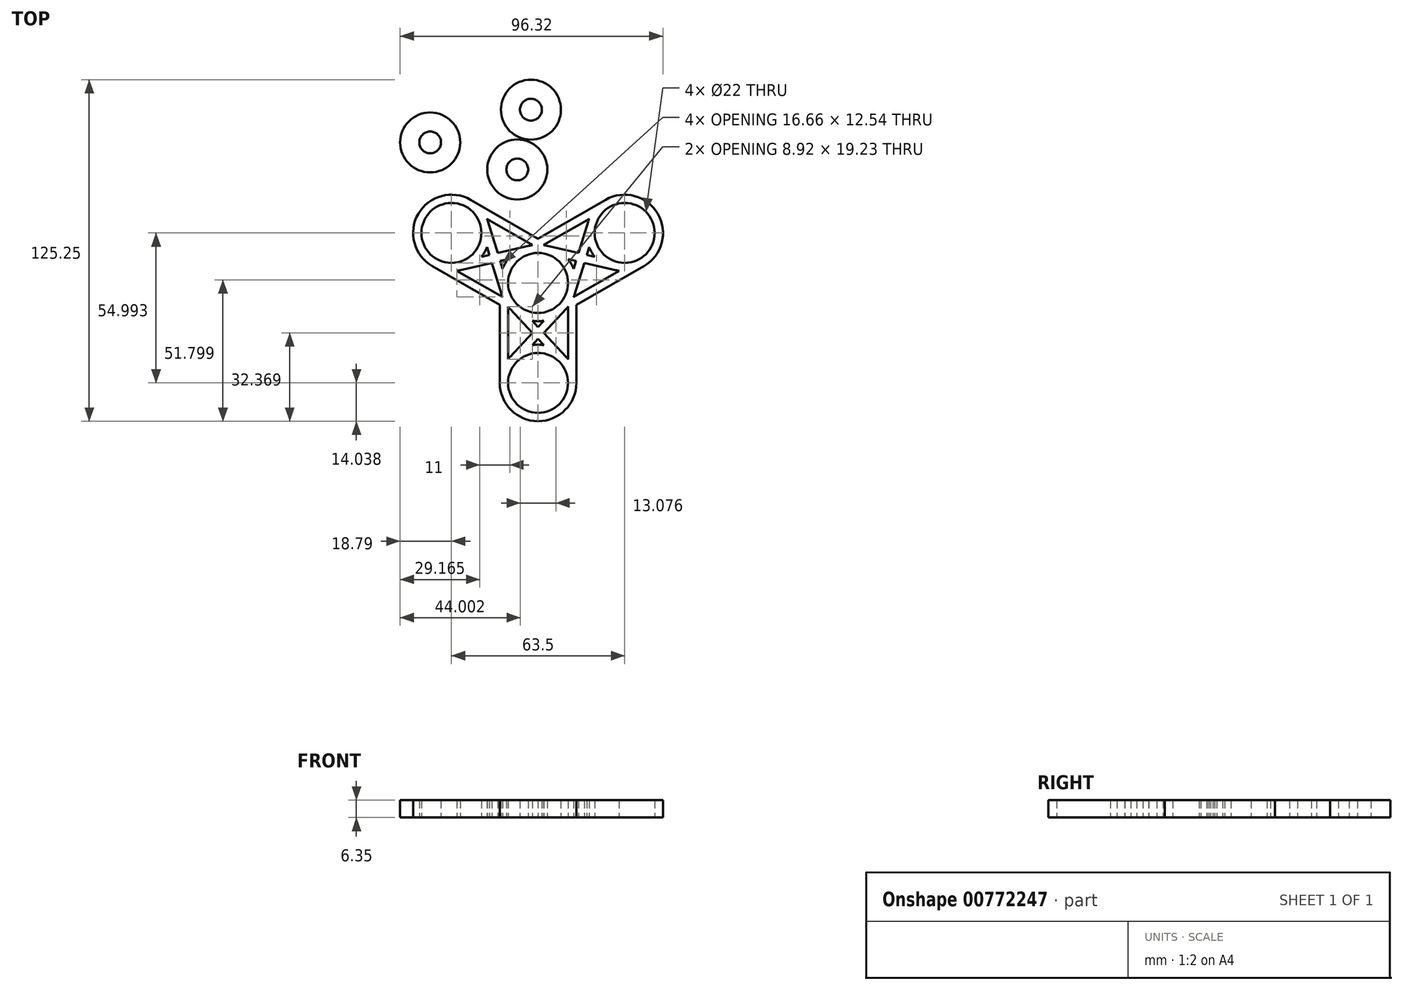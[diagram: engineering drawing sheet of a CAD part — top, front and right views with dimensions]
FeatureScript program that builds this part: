
annotation { "Feature Type Name" : "Feature", "Feature Type Description" : "" }
export const myFeature = defineFeature(function(context is Context, id is Id, definition is map)
    precondition{}
    {
        {
            var Q0;
            Q0=qCreatedBy(makeId("Top.planeOp"),FACE);
            var sketch = newSketch(context, id + "F0", { "sketchPlane" : qUnion([Q0])});
            skCircle(sketch, "E0", {"center": v(0, 0) * mm, "radius": 11 * mm});
            skCircle(sketch, "E1", {"center": v(0, 0) * mm, "radius": 4 * mm});
            skArc(sketch, "E2", {"start": v(-13.42, -4.09) * mm, "mid": v(-13.25, -4.63) * mm, "end": v(-13.05, -5.17) * mm});
            skCircle(sketch, "E3", {"center": v(31.75, 18.33) * mm, "radius": 11 * mm});
            skCircle(sketch, "E4", {"center": v(31.75, 18.33) * mm, "radius": 4 * mm});
            skArc(sketch, "E5", {"start": v(18.69, 13.2) * mm, "mid": v(19.6, 11.31) * mm, "end": v(20.77, 9.59) * mm});
            skCircle(sketch, "E6", {"center": v(-31.75, 18.33) * mm, "radius": 11 * mm});
            skCircle(sketch, "E7", {"center": v(-31.75, 18.33) * mm, "radius": 4 * mm});
            skArc(sketch, "E8", {"start": v(-18.33, 22.42) * mm, "mid": v(-18.5, 22.96) * mm, "end": v(-18.7, 23.5) * mm});
            skCircle(sketch, "E9", {"center": v(0, -36.66) * mm, "radius": 11 * mm});
            skCircle(sketch, "E10", {"center": v(0, -36.66) * mm, "radius": 4 * mm});
            skArc(sketch, "E11", {"start": v(-10.25, -27.08) * mm, "mid": v(-10.64, -27.5) * mm, "end": v(-11, -27.95) * mm});
            skLineSegment(sketch, "E12", {"start": v(-31.75, 18.33) * mm, "end": v(31.75, 18.33) * mm, "construction": true});
            skLineSegment(sketch, "E13", {"start": v(31.75, 18.33) * mm, "end": v(0, -36.66) * mm, "construction": true});
            skLineSegment(sketch, "E14", {"start": v(-31.75, 18.33) * mm, "end": v(0, -36.66) * mm, "construction": true});
            skLineSegment(sketch, "E15", {"start": v(0, 16.2) * mm, "end": v(24.73, 30.48) * mm});
            skLineSegment(sketch, "E16", {"start": v(-14.03, -8.1) * mm, "end": v(-14.03, -36.66) * mm});
            skLineSegment(sketch, "E17", {"start": v(11, -27.95) * mm, "end": v(11, -8.71) * mm});
            skLineSegment(sketch, "E18", {"start": v(14.03, -8.1) * mm, "end": v(38.77, 6.18) * mm});
            skLineSegment(sketch, "E19", {"start": v(-18.7, 23.5) * mm, "end": v(-2.05, 13.88) * mm});
            skLineSegment(sketch, "E20", {"start": v(14.03, -36.66) * mm, "end": v(14.03, -8.1) * mm});
            skLineSegment(sketch, "E21", {"start": v(-18.33, 22.42) * mm, "end": v(-14.84, 10.96) * mm});
            skLineSegment(sketch, "E22", {"start": v(-28.58, 4.66) * mm, "end": v(-16.91, 7.37) * mm});
            skLineSegment(sketch, "E23.trimOffspring", {"start": v(-13.95, 8.05) * mm, "end": v(-10.98, 8.75) * mm});
            skLineSegment(sketch, "E24.trimOffspring", {"start": v(-16.91, 7.37) * mm, "end": v(-13.42, -4.09) * mm});
            skLineSegment(sketch, "E25.trimOffspring", {"start": v(-13.95, 8.05) * mm, "end": v(-13.06, 5.13) * mm});
            skArc(sketch, "E26.trimOffspring", {"start": v(-20.77, 9.59) * mm, "mid": v(-19.6, 11.31) * mm, "end": v(-18.69, 13.2) * mm});
            skLineSegment(sketch, "E27.trimOffspring", {"start": v(-18.69, 13.2) * mm, "end": v(-17.8, 10.28) * mm});
            skArc(sketch, "E28.trimOffspring", {"start": v(-10.98, 8.75) * mm, "mid": v(-12.15, 7.02) * mm, "end": v(-13.06, 5.13) * mm});
            skArc(sketch, "E29.trimOffspring", {"start": v(-29.7, 4.45) * mm, "mid": v(-29.14, 4.54) * mm, "end": v(-28.58, 4.66) * mm});
            skLineSegment(sketch, "E30.trimOffspring", {"start": v(0, 16.2) * mm, "end": v(-24.73, 30.48) * mm});
            skArc(sketch, "E31.trimOffspring", {"start": v(-2.05, 13.88) * mm, "mid": v(-2.61, 13.79) * mm, "end": v(-3.17, 13.67) * mm});
            skLineSegment(sketch, "E32.trimOffspring", {"start": v(2.05, 13.88) * mm, "end": v(18.7, 23.5) * mm});
            skArc(sketch, "E33.trimOffspring", {"start": v(-11, -8.71) * mm, "mid": v(-10.64, -9.16) * mm, "end": v(-10.25, -9.58) * mm});
            skLineSegment(sketch, "E34.trimOffspring", {"start": v(-13.05, -5.17) * mm, "end": v(-29.7, 4.45) * mm});
            skLineSegment(sketch, "E35.trimOffspring", {"start": v(-11, -8.71) * mm, "end": v(-11, -27.95) * mm});
            skLineSegment(sketch, "E36.trimOffspring", {"start": v(-14.03, -8.1) * mm, "end": v(-38.77, 6.18) * mm});
            skLineSegment(sketch, "E37.trimOffspring", {"start": v(13.05, -5.17) * mm, "end": v(29.7, 4.45) * mm});
            skArc(sketch, "E38.trimOffspring", {"start": v(13.05, -5.17) * mm, "mid": v(13.25, -4.63) * mm, "end": v(13.42, -4.09) * mm});
            skLineSegment(sketch, "E39", {"start": v(13.06, 5.13) * mm, "end": v(13.95, 8.05) * mm});
            skLineSegment(sketch, "E40", {"start": v(3.17, 13.67) * mm, "end": v(14.84, 10.96) * mm});
            skLineSegment(sketch, "E41", {"start": v(10.98, 8.75) * mm, "end": v(13.95, 8.05) * mm});
            skLineSegment(sketch, "E42", {"start": v(10.25, -27.08) * mm, "end": v(2.08, -18.33) * mm});
            skLineSegment(sketch, "E43", {"start": v(-10.25, -27.08) * mm, "end": v(-2.08, -18.33) * mm});
            skLineSegment(sketch, "E44.trimOffspring", {"start": v(-20.77, 9.59) * mm, "end": v(-17.8, 10.28) * mm});
            skLineSegment(sketch, "E45.trimOffspring", {"start": v(-14.84, 10.96) * mm, "end": v(-3.17, 13.67) * mm});
            skArc(sketch, "E46.trimOffspring", {"start": v(-24.73, 30.48) * mm, "mid": v(-43.9, 25.35) * mm, "end": v(-38.77, 6.18) * mm});
            skLineSegment(sketch, "E47.trimOffspring", {"start": v(17.8, 10.28) * mm, "end": v(20.77, 9.59) * mm});
            skLineSegment(sketch, "E48.trimOffspring", {"start": v(16.91, 7.37) * mm, "end": v(28.58, 4.66) * mm});
            skLineSegment(sketch, "E49.trimOffspring", {"start": v(14.84, 10.96) * mm, "end": v(18.33, 22.42) * mm});
            skArc(sketch, "E50.trimOffspring", {"start": v(3.17, 13.67) * mm, "mid": v(2.61, 13.79) * mm, "end": v(2.05, 13.88) * mm});
            skArc(sketch, "E51.trimOffspring", {"start": v(13.06, 5.13) * mm, "mid": v(12.15, 7.02) * mm, "end": v(10.98, 8.75) * mm});
            skLineSegment(sketch, "E52.trimOffspring", {"start": v(16.91, 7.37) * mm, "end": v(13.42, -4.09) * mm});
            skLineSegment(sketch, "E53.trimOffspring", {"start": v(18.69, 13.2) * mm, "end": v(17.8, 10.28) * mm});
            skArc(sketch, "E54.trimOffspring", {"start": v(28.58, 4.66) * mm, "mid": v(29.14, 4.54) * mm, "end": v(29.7, 4.45) * mm});
            skArc(sketch, "E55.trimOffspring", {"start": v(38.77, 6.18) * mm, "mid": v(43.9, 25.35) * mm, "end": v(24.73, 30.48) * mm});
            skArc(sketch, "E56.trimOffspring", {"start": v(18.7, 23.5) * mm, "mid": v(18.5, 22.96) * mm, "end": v(18.33, 22.42) * mm});
            skArc(sketch, "E57.trimOffspring", {"start": v(-2.09, -13.88) * mm, "mid": v(0, -14.03) * mm, "end": v(2.09, -13.88) * mm});
            skArc(sketch, "E58.trimOffspring", {"start": v(10.25, -9.58) * mm, "mid": v(10.64, -9.16) * mm, "end": v(11, -8.71) * mm});
            skLineSegment(sketch, "E59.trimOffspring", {"start": v(0, -16.1) * mm, "end": v(2.09, -13.88) * mm});
            skLineSegment(sketch, "E60.trimOffspring", {"start": v(0, -16.1) * mm, "end": v(-2.09, -13.88) * mm});
            skLineSegment(sketch, "E61.trimOffspring", {"start": v(2.08, -18.33) * mm, "end": v(10.25, -9.58) * mm});
            skLineSegment(sketch, "E62.trimOffspring", {"start": v(-2.08, -18.33) * mm, "end": v(-10.25, -9.58) * mm});
            skLineSegment(sketch, "E63.trimOffspring", {"start": v(-2.09, -22.78) * mm, "end": v(0, -20.55) * mm});
            skLineSegment(sketch, "E64.trimOffspring", {"start": v(2.09, -22.78) * mm, "end": v(0, -20.55) * mm});
            skArc(sketch, "E65.trimOffspring", {"start": v(2.09, -22.78) * mm, "mid": v(0, -22.63) * mm, "end": v(-2.09, -22.78) * mm});
            skArc(sketch, "E66.trimOffspring", {"start": v(11, -27.95) * mm, "mid": v(10.64, -27.5) * mm, "end": v(10.25, -27.08) * mm});
            skArc(sketch, "E67.trimOffspring", {"start": v(-14.03, -36.66) * mm, "mid": v(0, -50.7) * mm, "end": v(14.03, -36.66) * mm});
            skLineSegment(sketch, "E68", {"start": v(31.75, 18.33) * mm, "end": v(0, 0) * mm, "construction": true});
            skLineSegment(sketch, "E69", {"start": v(-31.75, 18.33) * mm, "end": v(0, 0) * mm, "construction": true});
            skLineSegment(sketch, "E70", {"start": v(0, -36.66) * mm, "end": v(0, 0) * mm, "construction": true});
            skCircle(sketch, "E71", {"center": v(-39.54, 51.54) * mm, "radius": 11 * mm});
            skCircle(sketch, "E72", {"center": v(-39.54, 51.54) * mm, "radius": 4 * mm});
            skCircle(sketch, "E73", {"center": v(-7.62, 41.62) * mm, "radius": 11 * mm});
            skCircle(sketch, "E74", {"center": v(-7.62, 41.62) * mm, "radius": 4 * mm});
            skCircle(sketch, "E75", {"center": v(-2.62, 63.55) * mm, "radius": 11 * mm});
            skCircle(sketch, "E76", {"center": v(-2.62, 63.55) * mm, "radius": 4 * mm});
            skSolve(sketch);
        }
        {
            var Q0;
            Q0=qSketchRegion(id+"F0",true);
            extrude(context, id + "F1", {"entities" : qUnion([Q0]), "depth" : 6.35 * mm, "offsetDistance" : 25.4 * mm});
        }
    });
